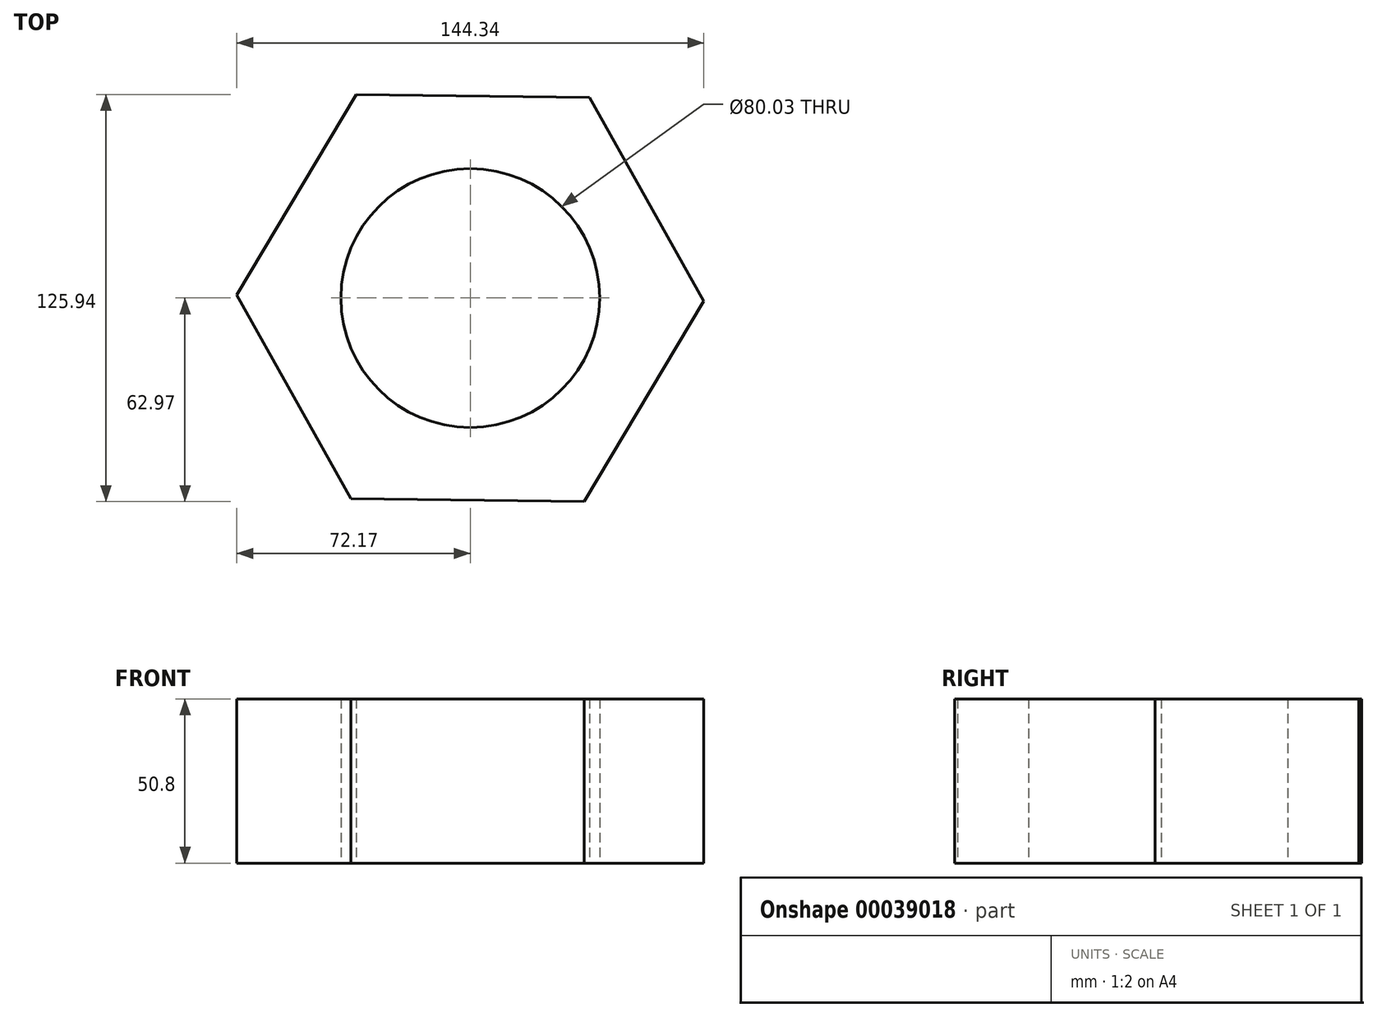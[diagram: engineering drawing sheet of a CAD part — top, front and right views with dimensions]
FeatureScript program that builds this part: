
annotation { "Feature Type Name" : "Feature", "Feature Type Description" : "" }
export const myFeature = defineFeature(function(context is Context, id is Id, definition is map)
    precondition{}
    {
        {
            var Q0;
            Q0=qCreatedBy(makeId("Top.planeOp"),FACE);
            var sketch = newSketch(context, id + "F0", { "sketchPlane" : qUnion([Q0])});
            skCircle(sketch, "E0.cCircle", {"center": v(0, 0) * mm, "radius": 62.5 * mm, "construction": true});
            skLineSegment(sketch, "E0.0", {"start": v(72.17, -0.93) * mm, "end": v(35.28, -62.97) * mm});
            skLineSegment(sketch, "E0.1", {"start": v(35.28, -62.97) * mm, "end": v(-36.9, -62.03) * mm});
            skLineSegment(sketch, "E0.2", {"start": v(-36.9, -62.03) * mm, "end": v(-72.17, 0.93) * mm});
            skLineSegment(sketch, "E0.3", {"start": v(-72.17, 0.93) * mm, "end": v(-35.28, 62.97) * mm});
            skLineSegment(sketch, "E0.4", {"start": v(-35.28, 62.97) * mm, "end": v(36.9, 62.03) * mm});
            skLineSegment(sketch, "E0.5", {"start": v(36.9, 62.03) * mm, "end": v(72.17, -0.93) * mm});
            skPoint(sketch, "E0.0.midPoint", {"position": v(53.72, -31.95) * mm});
            skCircle(sketch, "E1", {"center": v(0, 0) * mm, "radius": 40.02 * mm});
            skSolve(sketch);
        }
        {
            var Q0;
            Q0=makeQuery(id+"F0.imprint","IMPRINT",FACE,{"disambiguationData":[TD([[makeQuery(id+"F0.imprint","IMPRINT",EDGE,{"derivedFrom":sQuery(id+"F0.wireOp",EDGE,"E0.0")}),-1.0]])]});
            extrude(context, id + "F1", {"entities" : qUnion([Q0]), "depth" : 50.8 * mm});
        }
    });
